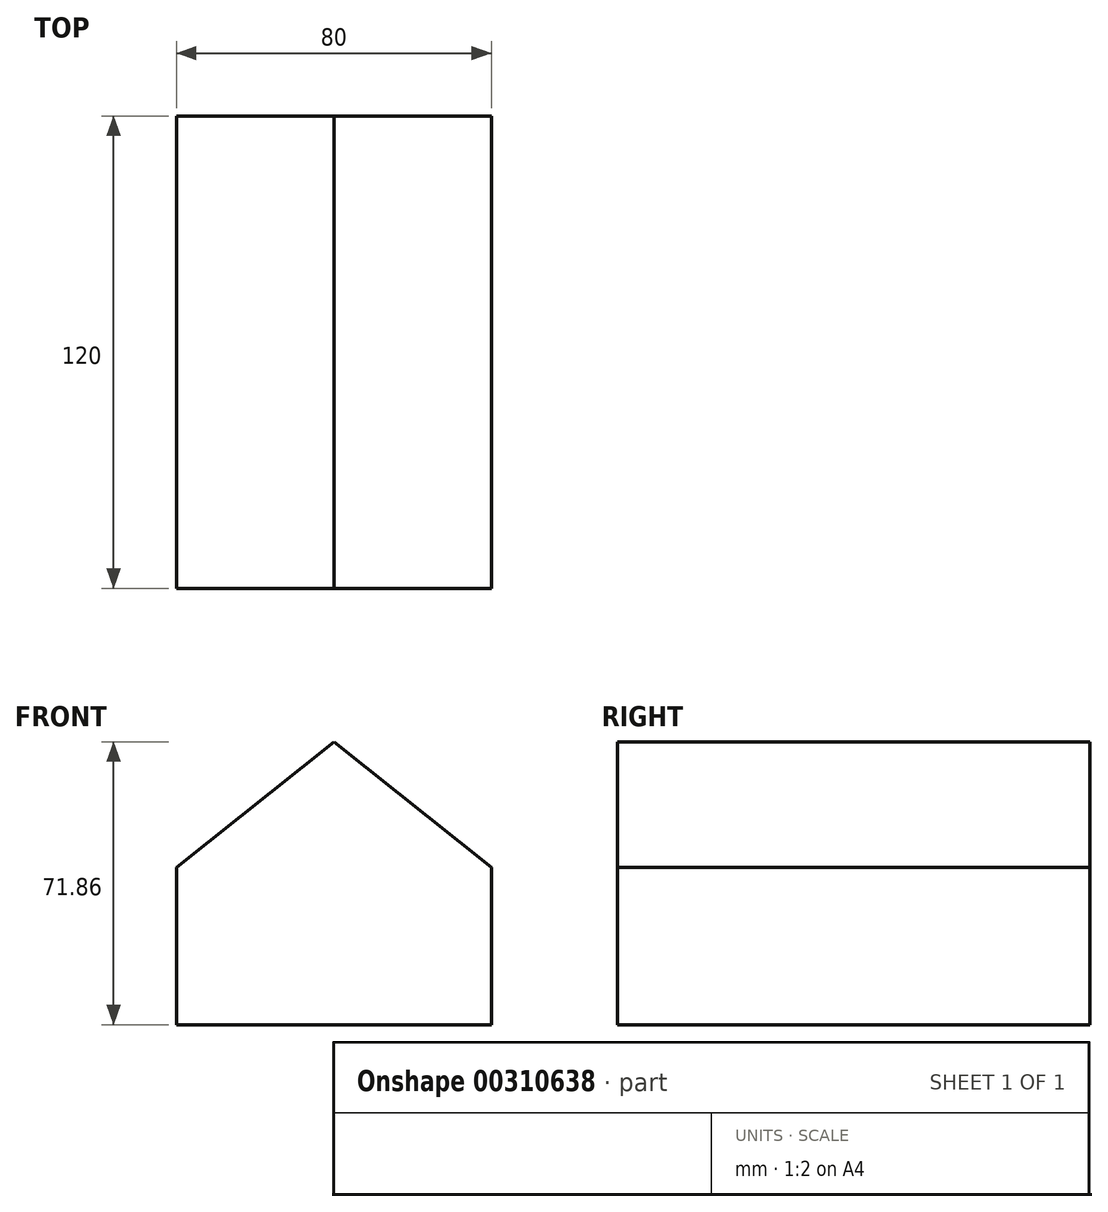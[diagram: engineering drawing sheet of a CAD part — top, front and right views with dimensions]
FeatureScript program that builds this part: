
annotation { "Feature Type Name" : "Feature", "Feature Type Description" : "" }
export const myFeature = defineFeature(function(context is Context, id is Id, definition is map)
    precondition{}
    {
        {
            var Q0;
            Q0=qCreatedBy(makeId("Front.planeOp"),FACE);
            var sketch = newSketch(context, id + "F0", { "sketchPlane" : qUnion([Q0])});
            skLineSegment(sketch, "E0", {"start": v(0, 0) * mm, "end": v(0, 40) * mm});
            skLineSegment(sketch, "E1", {"start": v(80, 40) * mm, "end": v(80, 0) * mm});
            skLineSegment(sketch, "E2", {"start": v(80, 0) * mm, "end": v(0, 0) * mm});
            skLineSegment(sketch, "E3", {"start": v(0, 40) * mm, "end": v(80, 40) * mm});
            skLineSegment(sketch, "E4", {"start": v(0, 40) * mm, "end": v(40, 71.86) * mm});
            skPoint(sketch, "E4.endSnap0", {"position": v(40, 40) * mm});
            skLineSegment(sketch, "E5", {"start": v(40, 71.86) * mm, "end": v(80, 40) * mm});
            skSolve(sketch);
        }
        {
            var Q0;
            Q0 = qSketchRegion(id + "F0", true);
            extrude(context, id + "F1", {"entities" : qUnion([Q0]), "depth" : 120 * mm});
        }
    });
